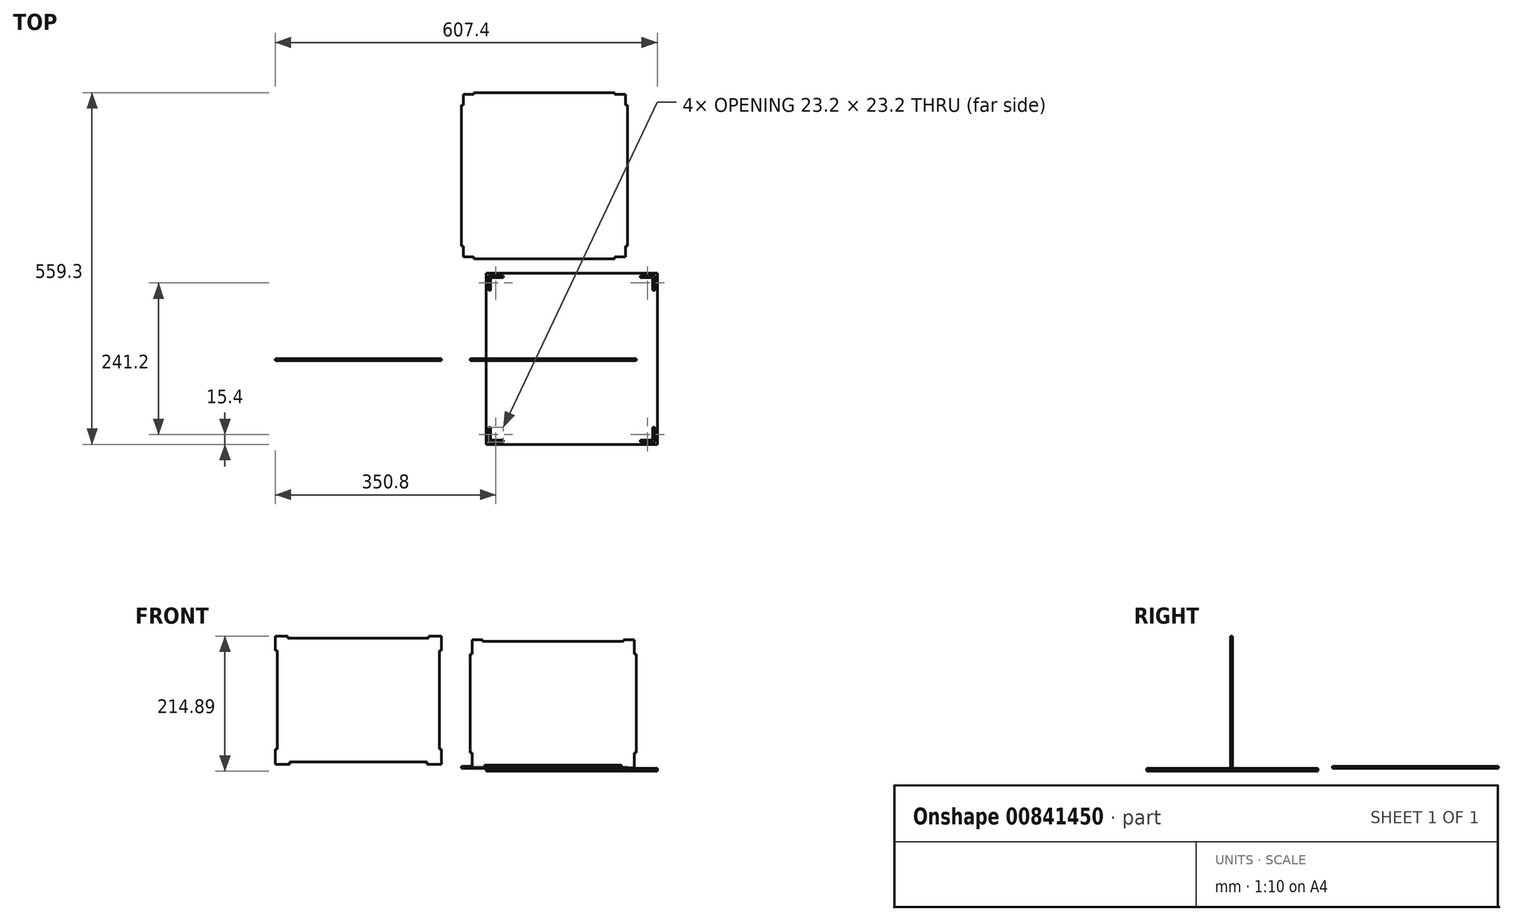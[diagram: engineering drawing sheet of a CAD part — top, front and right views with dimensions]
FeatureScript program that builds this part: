
annotation { "Feature Type Name" : "Feature", "Feature Type Description" : "" }
export const myFeature = defineFeature(function(context is Context, id is Id, definition is map)
    precondition{}
    {
        {
            var Q0;
            Q0=qCreatedBy(makeId("Top.planeOp"),FACE);
            var sketch = newSketch(context, id + "F0", { "sketchPlane" : qUnion([Q0])});
            skLineSegment(sketch, "E0.bottom", {"start": v(129, -129) * mm, "end": v(-129, -129) * mm, "construction": true});
            skLineSegment(sketch, "E0.top", {"start": v(129, 129) * mm, "end": v(-129, 129) * mm, "construction": true});
            skLineSegment(sketch, "E0.left", {"start": v(129, -129) * mm, "end": v(129, 129) * mm, "construction": true});
            skLineSegment(sketch, "E0.right", {"start": v(-129, -129) * mm, "end": v(-129, 129) * mm, "construction": true});
            skPoint(sketch, "E0.middle", {"position": v(0, 0) * mm});
            skLineSegment(sketch, "E1.bottom", {"start": v(136, -136) * mm, "end": v(-136, -136) * mm});
            skLineSegment(sketch, "E1.top", {"start": v(136, 136) * mm, "end": v(-136, 136) * mm});
            skLineSegment(sketch, "E1.left", {"start": v(136, -136) * mm, "end": v(136, 136) * mm});
            skLineSegment(sketch, "E1.right", {"start": v(-136, -136) * mm, "end": v(-136, 136) * mm});
            skLineSegment(sketch, "E2", {"start": v(-129, 109) * mm, "end": v(-132.2, 109) * mm});
            skLineSegment(sketch, "E3", {"start": v(-132.2, 109) * mm, "end": v(-132.2, 132.2) * mm});
            skLineSegment(sketch, "E4", {"start": v(-132.2, 132.2) * mm, "end": v(-109, 132.2) * mm});
            skLineSegment(sketch, "E5", {"start": v(-109, 132.2) * mm, "end": v(-109, 129) * mm});
            skLineSegment(sketch, "E6", {"start": v(-109, 129) * mm, "end": v(-129, 129) * mm});
            skLineSegment(sketch, "E7", {"start": v(-129, 109) * mm, "end": v(-129, 129) * mm});
            skLineSegment(sketch, "E8.1.0", {"start": v(-109, -132.2) * mm, "end": v(-132.2, -132.2) * mm});
            skLineSegment(sketch, "E8.1.1", {"start": v(-132.2, -132.2) * mm, "end": v(-132.2, -109) * mm});
            skLineSegment(sketch, "E8.1.2", {"start": v(-109, -129) * mm, "end": v(-129, -129) * mm});
            skLineSegment(sketch, "E8.1.3", {"start": v(-129, -109) * mm, "end": v(-129, -129) * mm});
            skLineSegment(sketch, "E8.1.4", {"start": v(-109, -129) * mm, "end": v(-109, -132.2) * mm});
            skLineSegment(sketch, "E8.1.5", {"start": v(-132.2, -109) * mm, "end": v(-129, -109) * mm});
            skLineSegment(sketch, "E8.2.0", {"start": v(132.2, -109) * mm, "end": v(132.2, -132.2) * mm});
            skLineSegment(sketch, "E8.2.1", {"start": v(132.2, -132.2) * mm, "end": v(109, -132.2) * mm});
            skLineSegment(sketch, "E8.2.2", {"start": v(129, -109) * mm, "end": v(129, -129) * mm});
            skLineSegment(sketch, "E8.2.3", {"start": v(109, -129) * mm, "end": v(129, -129) * mm});
            skLineSegment(sketch, "E8.2.4", {"start": v(129, -109) * mm, "end": v(132.2, -109) * mm});
            skLineSegment(sketch, "E8.2.5", {"start": v(109, -132.2) * mm, "end": v(109, -129) * mm});
            skLineSegment(sketch, "E8.3.0", {"start": v(109, 132.2) * mm, "end": v(132.2, 132.2) * mm});
            skLineSegment(sketch, "E8.3.1", {"start": v(132.2, 132.2) * mm, "end": v(132.2, 109) * mm});
            skLineSegment(sketch, "E8.3.2", {"start": v(109, 129) * mm, "end": v(129, 129) * mm});
            skLineSegment(sketch, "E8.3.3", {"start": v(129, 109) * mm, "end": v(129, 129) * mm});
            skLineSegment(sketch, "E8.3.4", {"start": v(109, 129) * mm, "end": v(109, 132.2) * mm});
            skLineSegment(sketch, "E8.3.5", {"start": v(132.2, 109) * mm, "end": v(129, 109) * mm});
            skSolve(sketch);
        }
        {
            var Q0;
            Q0 = qSketchRegion(id + "F0", true);
            extrude(context, id + "F1", {"entities" : qUnion([Q0]), "depth" : 4.5 * mm, "offsetDistance" : 25 * mm});
        }
        {
            var Q0;
            Q0=qCreatedBy(makeId("Front.planeOp"),FACE);
            var sketch = newSketch(context, id + "F2", { "sketchPlane" : qUnion([Q0])});
            skLineSegment(sketch, "E9.bottom", {"start": v(-138.6, 9.4) * mm, "end": v(79.4, 9.4) * mm});
            skLineSegment(sketch, "E9.top", {"start": v(-158.6, 209.4) * mm, "end": v(-141.6, 209.4) * mm});
            skLineSegment(sketch, "E9.left", {"start": v(-158.6, 9.4) * mm, "end": v(-158.6, 29.4) * mm});
            skLineSegment(sketch, "E9.right", {"start": v(99.4, 9.4) * mm, "end": v(99.4, 29.4) * mm});
            skLineSegment(sketch, "E10", {"start": v(-158.6, 9.4) * mm, "end": v(-158.6, 5.4) * mm});
            skLineSegment(sketch, "E11", {"start": v(-158.6, 5.4) * mm, "end": v(-138.6, 5.4) * mm});
            skLineSegment(sketch, "E12", {"start": v(-138.6, 5.4) * mm, "end": v(-138.6, 9.4) * mm});
            skLineSegment(sketch, "E13", {"start": v(99.4, 9.4) * mm, "end": v(99.4, 5.4) * mm});
            skLineSegment(sketch, "E14", {"start": v(99.4, 5.4) * mm, "end": v(79.4, 5.4) * mm});
            skLineSegment(sketch, "E15", {"start": v(79.4, 5.4) * mm, "end": v(79.4, 9.4) * mm});
            skLineSegment(sketch, "E16", {"start": v(-158.6, 186.4) * mm, "end": v(-161.6, 186.4) * mm});
            skLineSegment(sketch, "E17", {"start": v(-161.6, 186.4) * mm, "end": v(-161.6, 29.4) * mm});
            skLineSegment(sketch, "E18", {"start": v(-161.6, 29.4) * mm, "end": v(-158.6, 29.4) * mm});
            skLineSegment(sketch, "E19", {"start": v(99.4, 186.4) * mm, "end": v(102.4, 186.4) * mm});
            skLineSegment(sketch, "E20", {"start": v(102.4, 186.4) * mm, "end": v(102.4, 29.4) * mm});
            skLineSegment(sketch, "E21", {"start": v(102.4, 29.4) * mm, "end": v(99.4, 29.4) * mm});
            skLineSegment(sketch, "E22.trimOffspring", {"start": v(-158.6, 186.4) * mm, "end": v(-158.6, 209.4) * mm});
            skLineSegment(sketch, "E23.trimOffspring", {"start": v(99.4, 186.4) * mm, "end": v(99.4, 209.4) * mm});
            skLineSegment(sketch, "E24", {"start": v(-141.6, 209.4) * mm, "end": v(-141.6, 206.4) * mm});
            skLineSegment(sketch, "E25", {"start": v(-141.6, 206.4) * mm, "end": v(82.4, 206.4) * mm});
            skLineSegment(sketch, "E26", {"start": v(82.4, 206.4) * mm, "end": v(82.4, 209.4) * mm});
            skLineSegment(sketch, "E27.trimOffspring", {"start": v(82.4, 209.4) * mm, "end": v(99.4, 209.4) * mm});
            skSolve(sketch);
        }
        {
            var Q0;
            Q0 = qSketchRegion(id + "F2", true);
            extrude(context, id + "F3", {"entities" : qUnion([Q0]), "depth" : 3 * mm, "offsetDistance" : 25 * mm});
        }
        {
            var Q0;
            Q0=qCreatedBy(makeId("Front.planeOp"),FACE);
            var sketch = newSketch(context, id + "F4", { "sketchPlane" : qUnion([Q0])});
            skLineSegment(sketch, "E28.bottom", {"start": v(-448.4, 14.9) * mm, "end": v(-230.4, 14.9) * mm});
            skLineSegment(sketch, "E28.top", {"start": v(-471.4, 214.9) * mm, "end": v(-451.4, 214.9) * mm});
            skLineSegment(sketch, "E28.left", {"start": v(-471.4, 14.9) * mm, "end": v(-471.4, 34.9) * mm});
            skLineSegment(sketch, "E28.right", {"start": v(-207.4, 14.9) * mm, "end": v(-207.4, 34.9) * mm});
            skLineSegment(sketch, "E29", {"start": v(-451.4, 214.9) * mm, "end": v(-451.4, 211.9) * mm});
            skLineSegment(sketch, "E30", {"start": v(-451.4, 211.9) * mm, "end": v(-227.4, 211.9) * mm});
            skLineSegment(sketch, "E31", {"start": v(-227.4, 211.9) * mm, "end": v(-227.4, 214.9) * mm});
            skLineSegment(sketch, "E32.trimOffspring", {"start": v(-227.4, 214.9) * mm, "end": v(-207.4, 214.9) * mm});
            skLineSegment(sketch, "E33", {"start": v(-471.4, 191.9) * mm, "end": v(-468.4, 191.9) * mm});
            skLineSegment(sketch, "E34", {"start": v(-468.4, 191.9) * mm, "end": v(-468.4, 34.9) * mm});
            skLineSegment(sketch, "E35", {"start": v(-468.4, 34.9) * mm, "end": v(-471.4, 34.9) * mm});
            skLineSegment(sketch, "E36", {"start": v(-207.4, 191.9) * mm, "end": v(-210.4, 191.9) * mm});
            skLineSegment(sketch, "E37", {"start": v(-210.4, 191.9) * mm, "end": v(-210.4, 34.9) * mm});
            skLineSegment(sketch, "E38", {"start": v(-210.4, 34.9) * mm, "end": v(-207.4, 34.9) * mm});
            skLineSegment(sketch, "E39.trimOffspring", {"start": v(-471.4, 191.9) * mm, "end": v(-471.4, 214.9) * mm});
            skLineSegment(sketch, "E40.trimOffspring", {"start": v(-207.4, 191.9) * mm, "end": v(-207.4, 214.9) * mm});
            skLineSegment(sketch, "E41", {"start": v(-471.4, 14.9) * mm, "end": v(-471.4, 10.9) * mm});
            skLineSegment(sketch, "E42", {"start": v(-471.4, 10.9) * mm, "end": v(-448.4, 10.9) * mm});
            skLineSegment(sketch, "E43", {"start": v(-448.4, 10.9) * mm, "end": v(-448.4, 14.9) * mm});
            skLineSegment(sketch, "E44", {"start": v(-207.4, 14.9) * mm, "end": v(-207.4, 10.9) * mm});
            skLineSegment(sketch, "E45", {"start": v(-207.4, 10.9) * mm, "end": v(-230.4, 10.9) * mm});
            skLineSegment(sketch, "E46", {"start": v(-230.4, 10.9) * mm, "end": v(-230.4, 14.9) * mm});
            skSolve(sketch);
        }
        {
            var Q0;
            Q0 = qSketchRegion(id + "F4", true);
            extrude(context, id + "F5", {"entities" : qUnion([Q0]), "depth" : 3 * mm, "offsetDistance" : 25 * mm});
        }
        {
            var Q0;
            Q0=makeQuery(id+"F1.opExtrude","CAP_FACE",FACE,{"disambiguationData":[OSD([sQuery(id+"F0.wireOp",EDGE,"E1.bottom"),sQuery(id+"F0.wireOp",EDGE,"E1.top"),sQuery(id+"F0.wireOp",EDGE,"E1.left"),sQuery(id+"F0.wireOp",EDGE,"E1.right"),sQuery(id+"F0.wireOp",EDGE,"E2"),sQuery(id+"F0.wireOp",EDGE,"E3"),sQuery(id+"F0.wireOp",EDGE,"E4"),sQuery(id+"F0.wireOp",EDGE,"E5"),sQuery(id+"F0.wireOp",EDGE,"E6"),sQuery(id+"F0.wireOp",EDGE,"E7"),sQuery(id+"F0.wireOp",EDGE,"E8.1.0"),sQuery(id+"F0.wireOp",EDGE,"E8.1.1"),sQuery(id+"F0.wireOp",EDGE,"E8.1.2"),sQuery(id+"F0.wireOp",EDGE,"E8.1.3"),sQuery(id+"F0.wireOp",EDGE,"E8.1.4"),sQuery(id+"F0.wireOp",EDGE,"E8.1.5"),sQuery(id+"F0.wireOp",EDGE,"E8.2.0"),sQuery(id+"F0.wireOp",EDGE,"E8.2.1"),sQuery(id+"F0.wireOp",EDGE,"E8.2.2"),sQuery(id+"F0.wireOp",EDGE,"E8.2.3"),sQuery(id+"F0.wireOp",EDGE,"E8.2.4"),sQuery(id+"F0.wireOp",EDGE,"E8.2.5"),sQuery(id+"F0.wireOp",EDGE,"E8.3.0"),sQuery(id+"F0.wireOp",EDGE,"E8.3.1"),sQuery(id+"F0.wireOp",EDGE,"E8.3.2"),sQuery(id+"F0.wireOp",EDGE,"E8.3.3"),sQuery(id+"F0.wireOp",EDGE,"E8.3.4"),sQuery(id+"F0.wireOp",EDGE,"E8.3.5")])],"isStart":false});
            var sketch = newSketch(context, id + "F6", { "sketchPlane" : qUnion([Q0])});
            skLineSegment(sketch, "E47.bottom", {"start": v(-155.53, 423.3) * mm, "end": v(68.47, 423.3) * mm});
            skLineSegment(sketch, "E47.top", {"start": v(-155.53, 159.3) * mm, "end": v(68.47, 159.3) * mm});
            skLineSegment(sketch, "E47.left", {"start": v(-175.53, 403.3) * mm, "end": v(-175.53, 179.3) * mm});
            skLineSegment(sketch, "E47.right", {"start": v(88.47, 403.3) * mm, "end": v(88.47, 179.3) * mm});
            skLineSegment(sketch, "E48", {"start": v(-175.53, 403.3) * mm, "end": v(-172.53, 403.3) * mm});
            skLineSegment(sketch, "E49", {"start": v(-172.53, 403.3) * mm, "end": v(-172.53, 420.3) * mm});
            skLineSegment(sketch, "E50", {"start": v(-172.53, 420.3) * mm, "end": v(-155.53, 420.3) * mm});
            skLineSegment(sketch, "E51", {"start": v(-155.53, 420.3) * mm, "end": v(-155.53, 423.3) * mm});
            skPoint(sketch, "E52.orphan", {"position": v(-175.53, 423.3) * mm});
            skLineSegment(sketch, "E53", {"start": v(-175.53, 179.3) * mm, "end": v(-172.53, 179.3) * mm});
            skLineSegment(sketch, "E54", {"start": v(-172.53, 179.3) * mm, "end": v(-172.53, 162.3) * mm});
            skLineSegment(sketch, "E55", {"start": v(-172.53, 162.3) * mm, "end": v(-155.53, 162.3) * mm});
            skLineSegment(sketch, "E56", {"start": v(-155.53, 162.3) * mm, "end": v(-155.53, 159.3) * mm});
            skLineSegment(sketch, "E57", {"start": v(68.47, 159.3) * mm, "end": v(68.47, 162.3) * mm});
            skLineSegment(sketch, "E58", {"start": v(68.47, 162.3) * mm, "end": v(85.47, 162.3) * mm});
            skLineSegment(sketch, "E59", {"start": v(85.47, 162.3) * mm, "end": v(85.47, 179.3) * mm});
            skLineSegment(sketch, "E60", {"start": v(85.47, 179.3) * mm, "end": v(88.47, 179.3) * mm});
            skLineSegment(sketch, "E61", {"start": v(68.47, 423.3) * mm, "end": v(68.47, 420.3) * mm});
            skLineSegment(sketch, "E62", {"start": v(68.47, 420.3) * mm, "end": v(85.47, 420.3) * mm});
            skLineSegment(sketch, "E63", {"start": v(85.47, 420.3) * mm, "end": v(85.47, 403.3) * mm});
            skLineSegment(sketch, "E64", {"start": v(85.47, 403.3) * mm, "end": v(88.47, 403.3) * mm});
            skSolve(sketch);
        }
        {
            var Q0;
            Q0 = qSketchRegion(id + "F6", true);
            extrude(context, id + "F7", {"entities" : qUnion([Q0]), "depth" : 3 * mm, "offsetDistance" : 25 * mm});
        }
    });
